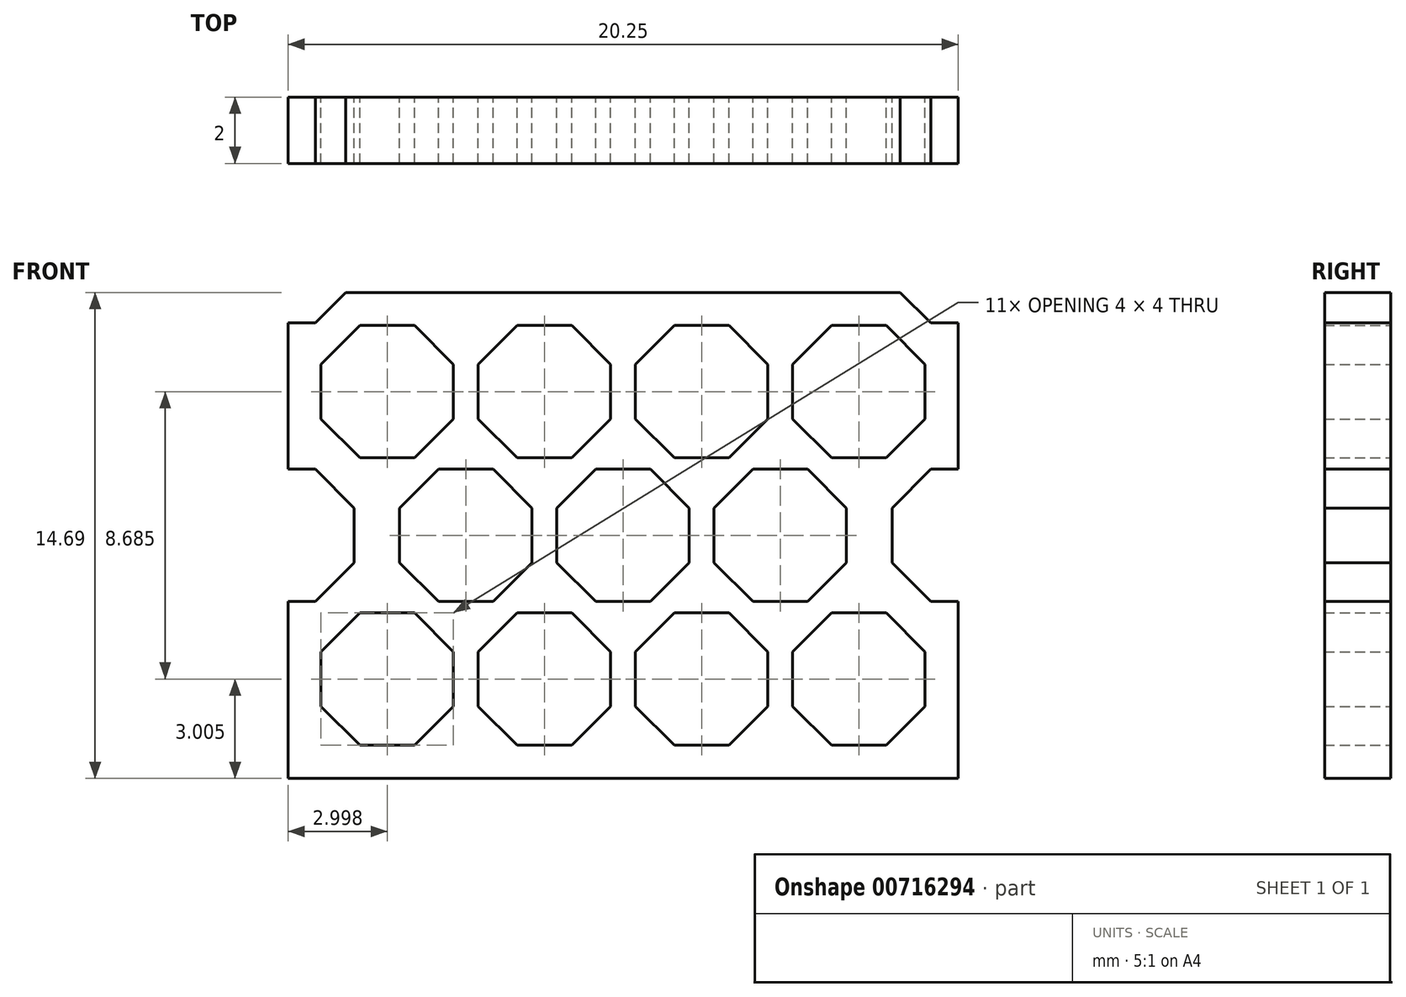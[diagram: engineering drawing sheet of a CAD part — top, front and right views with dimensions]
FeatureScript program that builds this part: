
annotation { "Feature Type Name" : "Feature", "Feature Type Description" : "" }
export const myFeature = defineFeature(function(context is Context, id is Id, definition is map)
    precondition{}
    {
        {
            var Q0;
            Q0=qCreatedBy(makeId("Front.planeOp"),FACE);
            var sketch = newSketch(context, id + "F0", { "sketchPlane" : qUnion([Q0])});
            skCircle(sketch, "E0.cCircle", {"center": v(-10.08, 8.33) * mm, "radius": 2 * mm, "construction": true});
            skLineSegment(sketch, "E0.0", {"start": v(-8.08, 7.5) * mm, "end": v(-9.25, 6.33) * mm});
            skLineSegment(sketch, "E0.1", {"start": v(-9.25, 6.33) * mm, "end": v(-10.91, 6.33) * mm});
            skLineSegment(sketch, "E0.2", {"start": v(-10.91, 6.33) * mm, "end": v(-12.08, 7.5) * mm});
            skLineSegment(sketch, "E0.3", {"start": v(-12.08, 7.5) * mm, "end": v(-12.08, 9.16) * mm});
            skLineSegment(sketch, "E0.4", {"start": v(-12.08, 9.16) * mm, "end": v(-10.91, 10.33) * mm});
            skLineSegment(sketch, "E0.5", {"start": v(-10.91, 10.33) * mm, "end": v(-9.25, 10.33) * mm});
            skLineSegment(sketch, "E0.6", {"start": v(-9.25, 10.33) * mm, "end": v(-8.08, 9.16) * mm});
            skLineSegment(sketch, "E0.7", {"start": v(-8.08, 9.16) * mm, "end": v(-8.08, 7.5) * mm});
            skPoint(sketch, "E0.0.midPoint", {"position": v(-8.67, 6.92) * mm});
            skLineSegment(sketch, "E1.1.0.0", {"start": v(-6.16, 10.33) * mm, "end": v(-4.5, 10.33) * mm});
            skPoint(sketch, "E1.1.0.1", {"position": v(-3.92, 6.92) * mm});
            skLineSegment(sketch, "E1.1.0.2", {"start": v(-7.33, 7.5) * mm, "end": v(-7.33, 9.16) * mm});
            skLineSegment(sketch, "E1.1.0.3", {"start": v(-6.16, 6.33) * mm, "end": v(-7.33, 7.5) * mm});
            skCircle(sketch, "E1.1.0.4", {"center": v(-5.33, 8.33) * mm, "radius": 2 * mm, "construction": true});
            skLineSegment(sketch, "E1.1.0.5", {"start": v(-3.33, 9.16) * mm, "end": v(-3.33, 7.5) * mm});
            skLineSegment(sketch, "E1.1.0.6", {"start": v(-4.5, 10.33) * mm, "end": v(-3.33, 9.16) * mm});
            skLineSegment(sketch, "E1.1.0.7", {"start": v(-7.33, 9.16) * mm, "end": v(-6.16, 10.33) * mm});
            skLineSegment(sketch, "E1.1.0.8", {"start": v(-4.5, 6.33) * mm, "end": v(-6.16, 6.33) * mm});
            skLineSegment(sketch, "E1.1.0.9", {"start": v(-3.33, 7.5) * mm, "end": v(-4.5, 6.33) * mm});
            skLineSegment(sketch, "E1.2.0.0", {"start": v(-1.41, 10.33) * mm, "end": v(0.25, 10.33) * mm});
            skPoint(sketch, "E1.2.0.1", {"position": v(0.83, 6.92) * mm});
            skLineSegment(sketch, "E1.2.0.2", {"start": v(-2.58, 7.5) * mm, "end": v(-2.58, 9.16) * mm});
            skLineSegment(sketch, "E1.2.0.3", {"start": v(-1.41, 6.33) * mm, "end": v(-2.58, 7.5) * mm});
            skCircle(sketch, "E1.2.0.4", {"center": v(-0.58, 8.33) * mm, "radius": 2 * mm, "construction": true});
            skLineSegment(sketch, "E1.2.0.5", {"start": v(1.42, 9.16) * mm, "end": v(1.42, 7.5) * mm});
            skLineSegment(sketch, "E1.2.0.6", {"start": v(0.25, 10.33) * mm, "end": v(1.42, 9.16) * mm});
            skLineSegment(sketch, "E1.2.0.7", {"start": v(-2.58, 9.16) * mm, "end": v(-1.41, 10.33) * mm});
            skLineSegment(sketch, "E1.2.0.8", {"start": v(0.25, 6.33) * mm, "end": v(-1.41, 6.33) * mm});
            skLineSegment(sketch, "E1.2.0.9", {"start": v(1.42, 7.5) * mm, "end": v(0.25, 6.33) * mm});
            skLineSegment(sketch, "E1.3.0.0", {"start": v(3.34, 10.33) * mm, "end": v(5, 10.33) * mm});
            skPoint(sketch, "E1.3.0.1", {"position": v(5.58, 6.92) * mm});
            skLineSegment(sketch, "E1.3.0.2", {"start": v(2.17, 7.5) * mm, "end": v(2.17, 9.16) * mm});
            skLineSegment(sketch, "E1.3.0.3", {"start": v(3.34, 6.33) * mm, "end": v(2.17, 7.5) * mm});
            skCircle(sketch, "E1.3.0.4", {"center": v(4.17, 8.33) * mm, "radius": 2 * mm, "construction": true});
            skLineSegment(sketch, "E1.3.0.5", {"start": v(6.17, 9.16) * mm, "end": v(6.17, 7.5) * mm});
            skLineSegment(sketch, "E1.3.0.6", {"start": v(5, 10.33) * mm, "end": v(6.17, 9.16) * mm});
            skLineSegment(sketch, "E1.3.0.7", {"start": v(2.17, 9.16) * mm, "end": v(3.34, 10.33) * mm});
            skLineSegment(sketch, "E1.3.0.8", {"start": v(5, 6.33) * mm, "end": v(3.34, 6.33) * mm});
            skLineSegment(sketch, "E1.3.0.9", {"start": v(6.17, 7.5) * mm, "end": v(5, 6.33) * mm});
            skLineSegment(sketch, "E1.direction1", {"start": v(-10.91, 6.33) * mm, "end": v(-6.16, 6.33) * mm, "construction": true});
            skLineSegment(sketch, "E2", {"start": v(-8.08, 7.5) * mm, "end": v(-7.33, 7.5) * mm, "construction": true});
            skLineSegment(sketch, "E3", {"start": v(-7.7, 7.5) * mm, "end": v(-7.7, 1.83) * mm, "construction": true});
            skCircle(sketch, "E4.cCircle", {"center": v(-7.7, 3.99) * mm, "radius": 2 * mm, "construction": true});
            skLineSegment(sketch, "E4.0", {"start": v(-9.7, 4.82) * mm, "end": v(-8.54, 5.99) * mm});
            skLineSegment(sketch, "E4.1", {"start": v(-8.54, 5.99) * mm, "end": v(-6.88, 5.99) * mm});
            skLineSegment(sketch, "E4.2", {"start": v(-6.88, 5.99) * mm, "end": v(-5.7, 4.82) * mm});
            skLineSegment(sketch, "E4.3", {"start": v(-5.7, 4.82) * mm, "end": v(-5.7, 3.16) * mm});
            skLineSegment(sketch, "E4.4", {"start": v(-5.7, 3.16) * mm, "end": v(-6.88, 1.99) * mm});
            skLineSegment(sketch, "E4.5", {"start": v(-6.88, 1.99) * mm, "end": v(-8.54, 1.99) * mm});
            skLineSegment(sketch, "E4.6", {"start": v(-8.54, 1.99) * mm, "end": v(-9.7, 3.16) * mm});
            skLineSegment(sketch, "E4.7", {"start": v(-9.7, 3.16) * mm, "end": v(-9.7, 4.82) * mm});
            skPoint(sketch, "E4.0.midPoint", {"position": v(-9.12, 5.4) * mm});
            skLineSegment(sketch, "E5.1.0.0", {"start": v(-2.13, 5.99) * mm, "end": v(-0.96, 4.82) * mm});
            skLineSegment(sketch, "E5.1.0.1", {"start": v(-2.96, 7.5) * mm, "end": v(-2.96, 1.83) * mm, "construction": true});
            skLineSegment(sketch, "E5.1.0.2", {"start": v(-4.96, 3.16) * mm, "end": v(-4.96, 4.82) * mm});
            skPoint(sketch, "E5.1.0.3", {"position": v(-4.37, 5.4) * mm});
            skLineSegment(sketch, "E5.1.0.4", {"start": v(-3.79, 1.99) * mm, "end": v(-4.96, 3.16) * mm});
            skLineSegment(sketch, "E5.1.0.5", {"start": v(-4.96, 4.82) * mm, "end": v(-3.79, 5.99) * mm});
            skLineSegment(sketch, "E5.1.0.6", {"start": v(-0.96, 3.16) * mm, "end": v(-2.13, 1.99) * mm});
            skLineSegment(sketch, "E5.1.0.7", {"start": v(-3.79, 5.99) * mm, "end": v(-2.13, 5.99) * mm});
            skLineSegment(sketch, "E5.1.0.8", {"start": v(-2.13, 1.99) * mm, "end": v(-3.79, 1.99) * mm});
            skLineSegment(sketch, "E5.1.0.9", {"start": v(-0.96, 4.82) * mm, "end": v(-0.96, 3.16) * mm});
            skCircle(sketch, "E5.1.0.10", {"center": v(-2.96, 3.99) * mm, "radius": 2 * mm, "construction": true});
            skLineSegment(sketch, "E5.2.0.0", {"start": v(2.62, 5.99) * mm, "end": v(3.8, 4.82) * mm});
            skLineSegment(sketch, "E5.2.0.1", {"start": v(1.8, 7.5) * mm, "end": v(1.8, 1.83) * mm, "construction": true});
            skLineSegment(sketch, "E5.2.0.2", {"start": v(-0.2, 3.16) * mm, "end": v(-0.2, 4.82) * mm});
            skPoint(sketch, "E5.2.0.3", {"position": v(0.38, 5.4) * mm});
            skLineSegment(sketch, "E5.2.0.4", {"start": v(0.96, 1.99) * mm, "end": v(-0.2, 3.16) * mm});
            skLineSegment(sketch, "E5.2.0.5", {"start": v(-0.2, 4.82) * mm, "end": v(0.96, 5.99) * mm});
            skLineSegment(sketch, "E5.2.0.6", {"start": v(3.8, 3.16) * mm, "end": v(2.62, 1.99) * mm});
            skLineSegment(sketch, "E5.2.0.7", {"start": v(0.96, 5.99) * mm, "end": v(2.62, 5.99) * mm});
            skLineSegment(sketch, "E5.2.0.8", {"start": v(2.62, 1.99) * mm, "end": v(0.96, 1.99) * mm});
            skLineSegment(sketch, "E5.2.0.9", {"start": v(3.8, 4.82) * mm, "end": v(3.8, 3.16) * mm});
            skCircle(sketch, "E5.2.0.10", {"center": v(1.8, 3.99) * mm, "radius": 2 * mm, "construction": true});
            skLineSegment(sketch, "E5.direction1", {"start": v(-7.7, 1.83) * mm, "end": v(-2.96, 1.83) * mm, "construction": true});
            skLineSegment(sketch, "E6", {"start": v(-10.08, 8.33) * mm, "end": v(-10.08, -2.39) * mm, "construction": true});
            skCircle(sketch, "E7.cCircle", {"center": v(-10.08, -0.36) * mm, "radius": 2 * mm, "construction": true});
            skLineSegment(sketch, "E7.0", {"start": v(-12.08, 0.47) * mm, "end": v(-10.91, 1.64) * mm});
            skLineSegment(sketch, "E7.1", {"start": v(-10.91, 1.64) * mm, "end": v(-9.25, 1.64) * mm});
            skLineSegment(sketch, "E7.2", {"start": v(-9.25, 1.64) * mm, "end": v(-8.08, 0.47) * mm});
            skLineSegment(sketch, "E7.3", {"start": v(-8.08, 0.47) * mm, "end": v(-8.08, -1.18) * mm});
            skLineSegment(sketch, "E7.4", {"start": v(-8.08, -1.18) * mm, "end": v(-9.25, -2.36) * mm});
            skLineSegment(sketch, "E7.5", {"start": v(-9.25, -2.36) * mm, "end": v(-10.91, -2.36) * mm});
            skLineSegment(sketch, "E7.6", {"start": v(-10.91, -2.36) * mm, "end": v(-12.08, -1.18) * mm});
            skLineSegment(sketch, "E7.7", {"start": v(-12.08, -1.18) * mm, "end": v(-12.08, 0.47) * mm});
            skPoint(sketch, "E7.0.midPoint", {"position": v(-11.5, 1.06) * mm});
            skLineSegment(sketch, "E8.1.0.0", {"start": v(-3.33, 0.47) * mm, "end": v(-3.33, -1.18) * mm});
            skLineSegment(sketch, "E8.1.0.1", {"start": v(-6.16, -2.36) * mm, "end": v(-7.33, -1.18) * mm});
            skLineSegment(sketch, "E8.1.0.2", {"start": v(-3.33, -1.18) * mm, "end": v(-4.5, -2.36) * mm});
            skPoint(sketch, "E8.1.0.3", {"position": v(-6.75, 1.06) * mm});
            skLineSegment(sketch, "E8.1.0.4", {"start": v(-4.5, 1.64) * mm, "end": v(-3.33, 0.47) * mm});
            skLineSegment(sketch, "E8.1.0.5", {"start": v(-7.33, -1.18) * mm, "end": v(-7.33, 0.47) * mm});
            skLineSegment(sketch, "E8.1.0.6", {"start": v(-4.5, -2.36) * mm, "end": v(-6.16, -2.36) * mm});
            skLineSegment(sketch, "E8.1.0.7", {"start": v(-6.16, 1.64) * mm, "end": v(-4.5, 1.64) * mm});
            skCircle(sketch, "E8.1.0.8", {"center": v(-5.33, -0.36) * mm, "radius": 2 * mm, "construction": true});
            skLineSegment(sketch, "E8.1.0.9", {"start": v(-7.33, 0.47) * mm, "end": v(-6.16, 1.64) * mm});
            skLineSegment(sketch, "E8.2.0.0", {"start": v(1.42, 0.47) * mm, "end": v(1.42, -1.18) * mm});
            skLineSegment(sketch, "E8.2.0.1", {"start": v(-1.41, -2.36) * mm, "end": v(-2.58, -1.18) * mm});
            skLineSegment(sketch, "E8.2.0.2", {"start": v(1.42, -1.18) * mm, "end": v(0.25, -2.36) * mm});
            skPoint(sketch, "E8.2.0.3", {"position": v(-2, 1.06) * mm});
            skLineSegment(sketch, "E8.2.0.4", {"start": v(0.25, 1.64) * mm, "end": v(1.42, 0.47) * mm});
            skLineSegment(sketch, "E8.2.0.5", {"start": v(-2.58, -1.18) * mm, "end": v(-2.58, 0.47) * mm});
            skLineSegment(sketch, "E8.2.0.6", {"start": v(0.25, -2.36) * mm, "end": v(-1.41, -2.36) * mm});
            skLineSegment(sketch, "E8.2.0.7", {"start": v(-1.41, 1.64) * mm, "end": v(0.25, 1.64) * mm});
            skCircle(sketch, "E8.2.0.8", {"center": v(-0.58, -0.36) * mm, "radius": 2 * mm, "construction": true});
            skLineSegment(sketch, "E8.2.0.9", {"start": v(-2.58, 0.47) * mm, "end": v(-1.41, 1.64) * mm});
            skLineSegment(sketch, "E8.3.0.0", {"start": v(6.17, 0.47) * mm, "end": v(6.17, -1.18) * mm});
            skLineSegment(sketch, "E8.3.0.1", {"start": v(3.34, -2.36) * mm, "end": v(2.17, -1.18) * mm});
            skLineSegment(sketch, "E8.3.0.2", {"start": v(6.17, -1.18) * mm, "end": v(5, -2.36) * mm});
            skPoint(sketch, "E8.3.0.3", {"position": v(2.75, 1.06) * mm});
            skLineSegment(sketch, "E8.3.0.4", {"start": v(5, 1.64) * mm, "end": v(6.17, 0.47) * mm});
            skLineSegment(sketch, "E8.3.0.5", {"start": v(2.17, -1.18) * mm, "end": v(2.17, 0.47) * mm});
            skLineSegment(sketch, "E8.3.0.6", {"start": v(5, -2.36) * mm, "end": v(3.34, -2.36) * mm});
            skLineSegment(sketch, "E8.3.0.7", {"start": v(3.34, 1.64) * mm, "end": v(5, 1.64) * mm});
            skCircle(sketch, "E8.3.0.8", {"center": v(4.17, -0.36) * mm, "radius": 2 * mm, "construction": true});
            skLineSegment(sketch, "E8.3.0.9", {"start": v(2.17, 0.47) * mm, "end": v(3.34, 1.64) * mm});
            skLineSegment(sketch, "E8.direction1", {"start": v(-10.91, -2.36) * mm, "end": v(-6.16, -2.36) * mm, "construction": true});
            skLineSegment(sketch, "E9.bottom", {"start": v(-13.08, 11.33) * mm, "end": v(7.17, 11.33) * mm});
            skLineSegment(sketch, "E9.top", {"start": v(-13.08, -3.36) * mm, "end": v(7.17, -3.36) * mm});
            skLineSegment(sketch, "E9.left", {"start": v(-13.08, 11.33) * mm, "end": v(-13.08, -3.36) * mm});
            skLineSegment(sketch, "E9.right", {"start": v(7.17, 11.33) * mm, "end": v(7.17, -3.36) * mm});
            skLineSegment(sketch, "E10", {"start": v(7.17, 3.99) * mm, "end": v(-13.08, 3.99) * mm, "construction": true});
            skCircle(sketch, "E11.cCircle", {"center": v(-13.08, 3.99) * mm, "radius": 2 * mm, "construction": true});
            skLineSegment(sketch, "E11.0", {"start": v(-11.08, 4.82) * mm, "end": v(-11.08, 3.16) * mm});
            skLineSegment(sketch, "E11.1", {"start": v(-11.08, 3.16) * mm, "end": v(-12.25, 1.99) * mm});
            skLineSegment(sketch, "E11.2", {"start": v(-12.25, 1.99) * mm, "end": v(-13.91, 1.99) * mm});
            skLineSegment(sketch, "E11.3", {"start": v(-13.91, 1.99) * mm, "end": v(-15.08, 3.16) * mm});
            skLineSegment(sketch, "E11.4", {"start": v(-15.08, 3.16) * mm, "end": v(-15.08, 4.82) * mm});
            skLineSegment(sketch, "E11.5", {"start": v(-15.08, 4.82) * mm, "end": v(-13.91, 5.99) * mm});
            skLineSegment(sketch, "E11.6", {"start": v(-13.91, 5.99) * mm, "end": v(-12.25, 5.99) * mm});
            skLineSegment(sketch, "E11.7", {"start": v(-12.25, 5.99) * mm, "end": v(-11.08, 4.82) * mm});
            skPoint(sketch, "E11.0.midPoint", {"position": v(-11.08, 3.99) * mm});
            skCircle(sketch, "E12.cCircle", {"center": v(7.17, 3.99) * mm, "radius": 2 * mm, "construction": true});
            skLineSegment(sketch, "E12.0", {"start": v(8, 5.99) * mm, "end": v(9.17, 4.82) * mm});
            skLineSegment(sketch, "E12.1", {"start": v(9.17, 4.82) * mm, "end": v(9.17, 3.16) * mm});
            skLineSegment(sketch, "E12.2", {"start": v(9.17, 3.16) * mm, "end": v(8, 1.99) * mm});
            skLineSegment(sketch, "E12.3", {"start": v(8, 1.99) * mm, "end": v(6.34, 1.99) * mm});
            skLineSegment(sketch, "E12.4", {"start": v(6.34, 1.99) * mm, "end": v(5.17, 3.16) * mm});
            skLineSegment(sketch, "E12.5", {"start": v(5.17, 3.16) * mm, "end": v(5.17, 4.82) * mm});
            skLineSegment(sketch, "E12.6", {"start": v(5.17, 4.82) * mm, "end": v(6.34, 5.99) * mm});
            skLineSegment(sketch, "E12.7", {"start": v(6.34, 5.99) * mm, "end": v(8, 5.99) * mm});
            skPoint(sketch, "E12.0.midPoint", {"position": v(8.58, 5.4) * mm});
            skLineSegment(sketch, "E13.1.0.0", {"start": v(-15.08, 11.58) * mm, "end": v(-15.08, 13.24) * mm});
            skLineSegment(sketch, "E13.1.0.1", {"start": v(-15.08, 13.24) * mm, "end": v(-13.91, 14.41) * mm});
            skLineSegment(sketch, "E13.1.0.2", {"start": v(-13.91, 14.41) * mm, "end": v(-12.26, 14.41) * mm});
            skLineSegment(sketch, "E13.1.0.3", {"start": v(-12.26, 10.41) * mm, "end": v(-13.91, 10.41) * mm});
            skLineSegment(sketch, "E13.1.0.4", {"start": v(-12.26, 14.41) * mm, "end": v(-11.08, 13.24) * mm});
            skLineSegment(sketch, "E13.1.0.5", {"start": v(-13.91, 10.41) * mm, "end": v(-15.08, 11.58) * mm});
            skCircle(sketch, "E13.1.0.6", {"center": v(-13.08, 12.41) * mm, "radius": 2 * mm, "construction": true});
            skPoint(sketch, "E13.1.0.7", {"position": v(-11.08, 12.41) * mm});
            skLineSegment(sketch, "E13.1.0.8", {"start": v(-11.08, 13.24) * mm, "end": v(-11.08, 11.58) * mm});
            skLineSegment(sketch, "E13.1.0.9", {"start": v(-11.08, 11.58) * mm, "end": v(-12.26, 10.41) * mm});
            skLineSegment(sketch, "E13.1.0.10", {"start": v(7.17, 12.41) * mm, "end": v(-13.08, 12.41) * mm, "construction": true});
            skLineSegment(sketch, "E13.1.0.11", {"start": v(5.17, 11.58) * mm, "end": v(5.17, 13.24) * mm});
            skLineSegment(sketch, "E13.1.0.12", {"start": v(9.17, 11.58) * mm, "end": v(8, 10.41) * mm});
            skLineSegment(sketch, "E13.1.0.13", {"start": v(8, 10.41) * mm, "end": v(6.34, 10.41) * mm});
            skLineSegment(sketch, "E13.1.0.14", {"start": v(9.17, 13.24) * mm, "end": v(9.17, 11.58) * mm});
            skPoint(sketch, "E13.1.0.15", {"position": v(8.58, 13.83) * mm});
            skCircle(sketch, "E13.1.0.16", {"center": v(7.17, 12.41) * mm, "radius": 2 * mm, "construction": true});
            skLineSegment(sketch, "E13.1.0.17", {"start": v(8, 14.41) * mm, "end": v(9.17, 13.24) * mm});
            skLineSegment(sketch, "E13.1.0.18", {"start": v(6.34, 10.41) * mm, "end": v(5.17, 11.58) * mm});
            skLineSegment(sketch, "E13.1.0.19", {"start": v(7.17, 19.75) * mm, "end": v(7.17, 5.07) * mm});
            skLineSegment(sketch, "E13.1.0.20", {"start": v(5.17, 13.24) * mm, "end": v(6.34, 14.41) * mm});
            skLineSegment(sketch, "E13.1.0.21", {"start": v(6.34, 14.41) * mm, "end": v(8, 14.41) * mm});
            skLineSegment(sketch, "E13.2.0.0", {"start": v(-15.09, 20) * mm, "end": v(-15.09, 21.67) * mm});
            skLineSegment(sketch, "E13.2.0.1", {"start": v(-15.09, 21.67) * mm, "end": v(-13.91, 22.84) * mm});
            skLineSegment(sketch, "E13.2.0.2", {"start": v(-13.91, 22.84) * mm, "end": v(-12.26, 22.84) * mm});
            skLineSegment(sketch, "E13.2.0.3", {"start": v(-12.26, 18.84) * mm, "end": v(-13.91, 18.84) * mm});
            skLineSegment(sketch, "E13.2.0.4", {"start": v(-12.26, 22.84) * mm, "end": v(-11.09, 21.67) * mm});
            skLineSegment(sketch, "E13.2.0.5", {"start": v(-13.91, 18.84) * mm, "end": v(-15.09, 20) * mm});
            skCircle(sketch, "E13.2.0.6", {"center": v(-13.09, 20.84) * mm, "radius": 2 * mm, "construction": true});
            skPoint(sketch, "E13.2.0.7", {"position": v(-11.09, 20.84) * mm});
            skLineSegment(sketch, "E13.2.0.8", {"start": v(-11.09, 21.67) * mm, "end": v(-11.09, 20) * mm});
            skLineSegment(sketch, "E13.2.0.9", {"start": v(-11.09, 20) * mm, "end": v(-12.26, 18.84) * mm});
            skLineSegment(sketch, "E13.2.0.10", {"start": v(7.16, 20.84) * mm, "end": v(-13.09, 20.84) * mm, "construction": true});
            skLineSegment(sketch, "E13.2.0.11", {"start": v(5.16, 20) * mm, "end": v(5.16, 21.67) * mm});
            skLineSegment(sketch, "E13.2.0.12", {"start": v(9.16, 20) * mm, "end": v(8, 18.84) * mm});
            skLineSegment(sketch, "E13.2.0.13", {"start": v(8, 18.84) * mm, "end": v(6.34, 18.84) * mm});
            skLineSegment(sketch, "E13.2.0.14", {"start": v(9.16, 21.67) * mm, "end": v(9.16, 20) * mm});
            skPoint(sketch, "E13.2.0.15", {"position": v(8.58, 22.25) * mm});
            skCircle(sketch, "E13.2.0.16", {"center": v(7.16, 20.84) * mm, "radius": 2 * mm, "construction": true});
            skLineSegment(sketch, "E13.2.0.17", {"start": v(8, 22.84) * mm, "end": v(9.16, 21.67) * mm});
            skLineSegment(sketch, "E13.2.0.18", {"start": v(6.34, 18.84) * mm, "end": v(5.16, 20) * mm});
            skLineSegment(sketch, "E13.2.0.19", {"start": v(7.16, 28.18) * mm, "end": v(7.16, 13.5) * mm});
            skLineSegment(sketch, "E13.2.0.20", {"start": v(5.16, 21.67) * mm, "end": v(6.34, 22.84) * mm});
            skLineSegment(sketch, "E13.2.0.21", {"start": v(6.34, 22.84) * mm, "end": v(8, 22.84) * mm});
            skLineSegment(sketch, "E13.direction1", {"start": v(-13.91, 1.99) * mm, "end": v(-13.91, 10.41) * mm, "construction": true});
            skSolve(sketch);
        }
        {
            var Q0;
            Q0=makeQuery(id+"F0.imprint","IMPRINT",FACE,{"disambiguationData":[TD([[makeQuery(id+"F0.imprint","IMPRINT",EDGE,{"derivedFrom":sQuery(id+"F0.wireOp",EDGE,"E0.0")}),1.0]])]});
            extrude(context, id + "F1", {"entities" : qUnion([Q0]), "depth" : 2 * mm, "offsetDistance" : 25 * mm});
        }
    });
